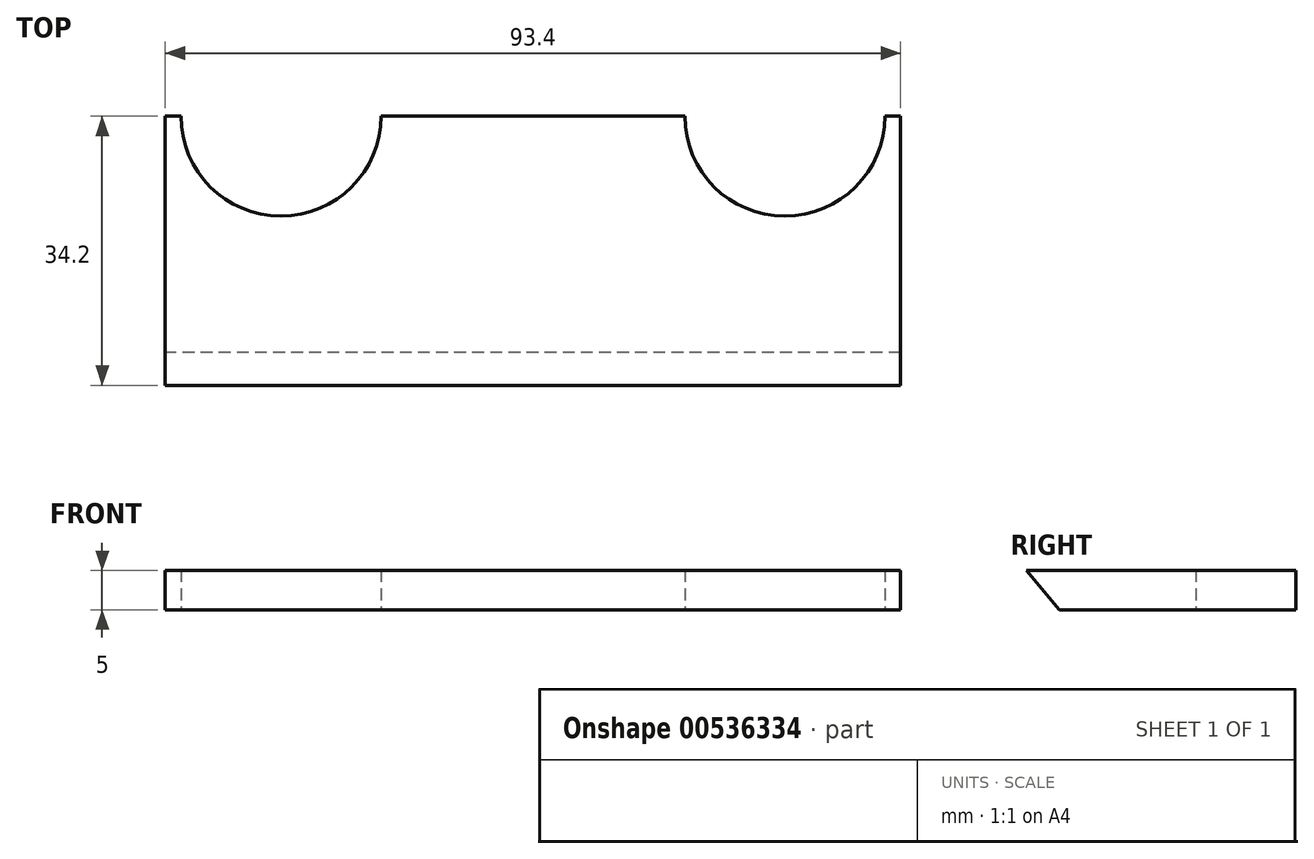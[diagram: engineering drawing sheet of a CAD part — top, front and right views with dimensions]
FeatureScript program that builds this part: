
annotation { "Feature Type Name" : "Feature", "Feature Type Description" : "" }
export const myFeature = defineFeature(function(context is Context, id is Id, definition is map)
    precondition{}
    {
        {
            var Q0;
            Q0=qCreatedBy(makeId("Top.planeOp"),FACE);
            var sketch = newSketch(context, id + "F0", { "sketchPlane" : qUnion([Q0])});
            skLineSegment(sketch, "E0.bottom", {"start": v(0, 0) * mm, "end": v(-46.7, 0) * mm});
            skLineSegment(sketch, "E0.top", {"start": v(0, 30) * mm, "end": v(-19.3, 30) * mm});
            skLineSegment(sketch, "E0.left", {"start": v(0, 0) * mm, "end": v(0, 30) * mm});
            skLineSegment(sketch, "E0.right", {"start": v(-46.7, 0) * mm, "end": v(-46.7, 30) * mm});
            skArc(sketch, "E1", {"start": v(-44.7, 30) * mm, "mid": v(-32, 17.3) * mm, "end": v(-19.3, 30) * mm});
            skLineSegment(sketch, "E2.MirrorCS", {"start": v(46.7, 0) * mm, "end": v(46.7, 30) * mm});
            skLineSegment(sketch, "E3.MirrorCS", {"start": v(0, 30) * mm, "end": v(19.3, 30) * mm});
            skArc(sketch, "E4.MirrorC", {"start": v(44.7, 30) * mm, "mid": v(32, 17.3) * mm, "end": v(19.3, 30) * mm});
            skLineSegment(sketch, "E5.MirrorCS", {"start": v(0, 0) * mm, "end": v(46.7, 0) * mm});
            skPoint(sketch, "E6", {"position": v(-19.3, 30) * mm});
            skPoint(sketch, "E7", {"position": v(19.3, 30) * mm});
            skPoint(sketch, "E8", {"position": v(-44.7, 30) * mm});
            skLineSegment(sketch, "E9.trimOffspring", {"start": v(-44.7, 30) * mm, "end": v(-46.7, 30) * mm});
            skLineSegment(sketch, "E10.trimOffspring", {"start": v(44.7, 30) * mm, "end": v(46.7, 30) * mm});
            skSolve(sketch);
        }
        {
            var Q0;
            Q0 = qSketchRegion(id + "F0", true);
            extrude(context, id + "F1", {"entities" : qUnion([Q0]), "depth" : 5 * mm, "offsetDistance" : 25 * mm});
        }
        {
            var Q0;
            Q0=makeQuery(id+"F1.opExtrude","SWEPT_FACE",FACE,{"disambiguationData":[OSD([sQuery(id+"F0.wireOp",EDGE,"E0.right")])]});
            var sketch = newSketch(context, id + "F2", { "sketchPlane" : qUnion([Q0])});
            skLineSegment(sketch, "E11", {"start": v(0, 0) * mm, "end": v(4.2, 5) * mm});
            skLineSegment(sketch, "E12", {"start": v(0, 5) * mm, "end": v(0, 0) * mm});
            skLineSegment(sketch, "E13", {"start": v(0, 5) * mm, "end": v(4.2, 5) * mm});
            skSolve(sketch);
        }
        {
            var Q0;
            Q0 = qSketchRegion(id + "F2", true);
            var Q1;
            Q1=makeQuery(id+"F1.opExtrude","SWEPT_FACE",FACE,{"disambiguationData":[OSD([sQuery(id+"F0.wireOp",EDGE,"E2.MirrorCS")])]});
            extrude(context, id + "F3", {"entities" : qUnion([Q0]), "operationType" : NewBodyOperationType.ADD, "endBound" : BoundingType.UP_TO_SURFACE, "oppositeDirection" : true, "depth" : 25 * mm, "endBoundEntityFace" : qUnion([Q1]), "offsetDistance" : 25 * mm});
        }
    });
